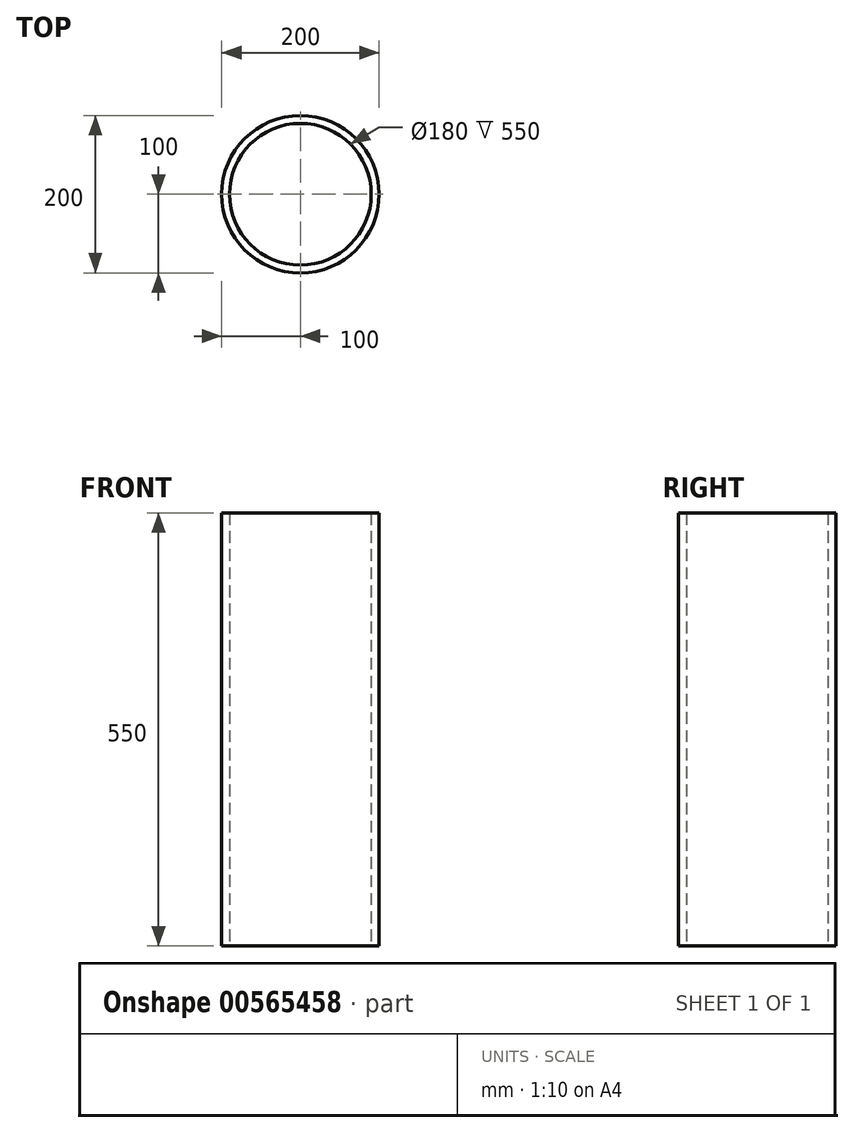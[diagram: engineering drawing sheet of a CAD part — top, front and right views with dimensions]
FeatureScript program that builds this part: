
annotation { "Feature Type Name" : "Feature", "Feature Type Description" : "" }
export const myFeature = defineFeature(function(context is Context, id is Id, definition is map)
    precondition{}
    {
        {
            var Q0;
            Q0=qCreatedBy(makeId("Top.planeOp"),FACE);
            var sketch = newSketch(context, id + "F0", { "sketchPlane" : qUnion([Q0])});
            skCircle(sketch, "E0", {"center": v(0, 0) * mm, "radius": 100 * mm});
            skCircle(sketch, "E1.0", {"center": v(0, 0) * mm, "radius": 90 * mm});
            skSolve(sketch);
        }
        {
            var Q0;
            Q0=makeQuery(id+"F0.imprint","IMPRINT",FACE,{"disambiguationData":[TD([[makeQuery(id+"F0.imprint","IMPRINT",EDGE,{"derivedFrom":sQuery(id+"F0.wireOp",EDGE,"E0")}),1.0]])]});
            extrude(context, id + "F1", {"entities" : qUnion([Q0]), "depth" : 550 * mm, "offsetDistance" : 25 * mm});
        }
    });
